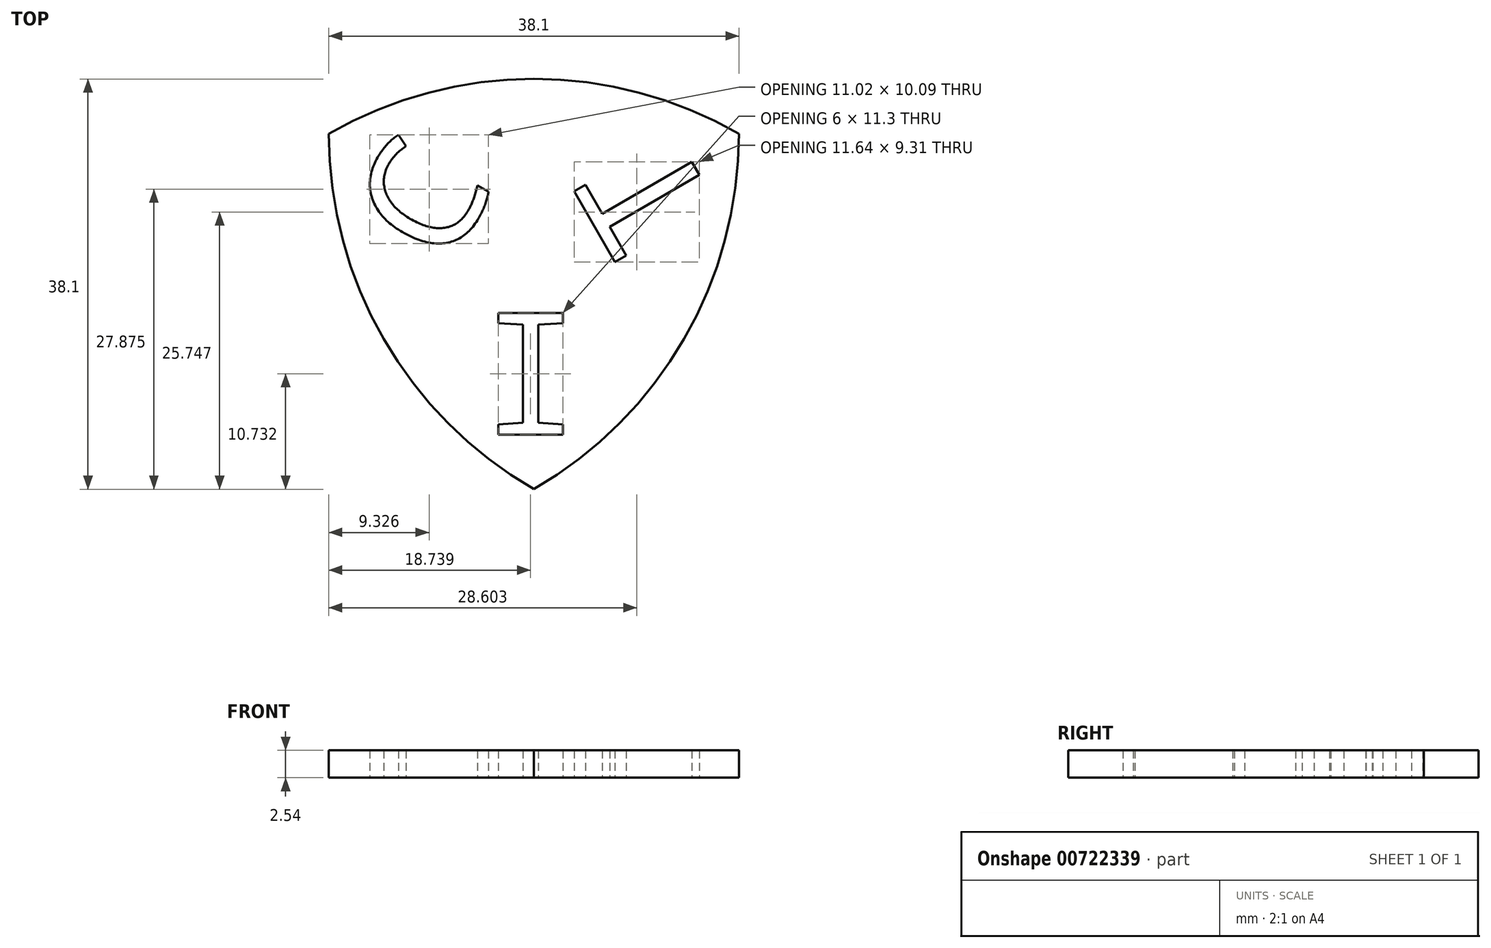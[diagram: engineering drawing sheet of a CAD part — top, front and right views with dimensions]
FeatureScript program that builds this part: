
annotation { "Feature Type Name" : "Feature", "Feature Type Description" : "" }
export const myFeature = defineFeature(function(context is Context, id is Id, definition is map)
    precondition{}
    {
        {
            var Q0;
            Q0=qCreatedBy(makeId("Top.planeOp"),FACE);
            var sketch = newSketch(context, id + "F0", { "sketchPlane" : qUnion([Q0])});
            skCircle(sketch, "E0", {"center": v(0, 0) * mm, "radius": 38.1 * mm});
            skSolve(sketch);
        }
        {
            var Q0;
            Q0=qCreatedBy(makeId("Top.planeOp"),FACE);
            var sketch = newSketch(context, id + "F1", { "sketchPlane" : qUnion([Q0])});
            skCircle(sketch, "E1", {"center": v(-38.1, 0) * mm, "radius": 38.1 * mm});
            skSolve(sketch);
        }
        {
            var Q0;
            Q0=qCreatedBy(makeId("Top.planeOp"),FACE);
            var sketch = newSketch(context, id + "F2", { "sketchPlane" : qUnion([Q0])});
            skCircle(sketch, "E2", {"center": v(-19.05, -33) * mm, "radius": 38.1 * mm});
            skSolve(sketch);
        }
        {
            var Q0;
            Q0 = qSketchRegion(id + "F0", true);
            extrude(context, id + "F3", {"entities" : qUnion([Q0]), "depth" : 2.54 * mm, "offsetDistance" : 25.4 * mm});
        }
        {
            var Q0;
            Q0 = qSketchRegion(id + "F1", true);
            extrude(context, id + "F4", {"entities" : qUnion([Q0]), "depth" : 2.54 * mm, "offsetDistance" : 25.4 * mm});
        }
        {
            var Q0;
            Q0 = qSketchRegion(id + "F2", true);
            extrude(context, id + "F5", {"entities" : qUnion([Q0]), "depth" : 2.54 * mm, "offsetDistance" : 25.4 * mm});
        }
        {
            var Q0;
            Q0=makeQuery(id+"F5.opExtrude","SWEPT_BODY",BODY,{"disambiguationData":[OSD([sQuery(id+"F2.wireOp",EDGE,"E2")])]});
            var Q1;
            Q1=makeQuery(id+"F4.opExtrude","SWEPT_BODY",BODY,{"disambiguationData":[OSD([sQuery(id+"F1.wireOp",EDGE,"E1")])]});
            var Q2;
            Q2=makeQuery(id+"F3.opExtrude","SWEPT_BODY",BODY,{"disambiguationData":[OSD([sQuery(id+"F0.wireOp",EDGE,"E0")])]});
            booleanBodies(context, id + "F6", {"operationType" : BooleanOperationType.INTERSECTION, "tools" : qUnion([Q0, Q1, Q2])});
        }
        {
            var Q0;
            Q0=qCreatedBy(makeId("Top.planeOp"),FACE);
            var sketch = newSketch(context, id + "F7", { "sketchPlane" : qUnion([Q0])});
            skText(sketch, "E3", { "text": "C", "fontName": "DroidSansMono.ttf"});
            skText(sketch, "E4", { "text": "I", "fontName": "DroidSansMono.ttf"});
            skText(sketch, "E5", { "text": "T", "fontName": "DroidSansMono.ttf"});
            const initialGuessF7  = {"E3": [-0.02711, -0.0126, 0.5, 0.86603, 0.01073], "E4": [-0.0241, -0.02792, 1, 0, 0.0114], "E5": [-0.00175, -0.00714, -0.5, 0.86603, 0.01094]};
            skSetInitialGuess(sketch, initialGuessF7);
            skSolve(sketch);
        }
        {
            var Q0;
            Q0 = qSketchRegion(id + "F7", true);
            extrude(context, id + "F8", {"entities" : qUnion([Q0]), "depth" : 2.54 * mm, "offsetDistance" : 25.4 * mm});
        }
        {
            var Q0;
            Q0=makeQuery(id+"F8.opExtrude","SWEPT_BODY",BODY,{"disambiguationData":[OSD([sQuery(id+"F7.wireOp",EDGE,"E3.sketch_text.stroke-0"),sQuery(id+"F7.wireOp",EDGE,"E3.sketch_text.stroke-1"),sQuery(id+"F7.wireOp",EDGE,"E3.sketch_text.stroke-2"),sQuery(id+"F7.wireOp",EDGE,"E3.sketch_text.stroke-3"),sQuery(id+"F7.wireOp",EDGE,"E3.sketch_text.stroke-4"),sQuery(id+"F7.wireOp",EDGE,"E3.sketch_text.stroke-5"),sQuery(id+"F7.wireOp",EDGE,"E3.sketch_text.stroke-6"),sQuery(id+"F7.wireOp",EDGE,"E3.sketch_text.stroke-7"),sQuery(id+"F7.wireOp",EDGE,"E3.sketch_text.stroke-8"),sQuery(id+"F7.wireOp",EDGE,"E3.sketch_text.stroke-9"),sQuery(id+"F7.wireOp",EDGE,"E3.sketch_text.stroke-10"),sQuery(id+"F7.wireOp",EDGE,"E3.sketch_text.stroke-11"),sQuery(id+"F7.wireOp",EDGE,"E3.sketch_text.stroke-12"),sQuery(id+"F7.wireOp",EDGE,"E3.sketch_text.stroke-13")])]});
            var Q1;
            Q1=makeQuery(id+"F8.opExtrude","SWEPT_BODY",BODY,{"disambiguationData":[OSD([sQuery(id+"F7.wireOp",EDGE,"E4.sketch_text.stroke-0"),sQuery(id+"F7.wireOp",EDGE,"E4.sketch_text.stroke-1"),sQuery(id+"F7.wireOp",EDGE,"E4.sketch_text.stroke-2"),sQuery(id+"F7.wireOp",EDGE,"E4.sketch_text.stroke-3"),sQuery(id+"F7.wireOp",EDGE,"E4.sketch_text.stroke-4"),sQuery(id+"F7.wireOp",EDGE,"E4.sketch_text.stroke-5"),sQuery(id+"F7.wireOp",EDGE,"E4.sketch_text.stroke-6"),sQuery(id+"F7.wireOp",EDGE,"E4.sketch_text.stroke-7"),sQuery(id+"F7.wireOp",EDGE,"E4.sketch_text.stroke-8"),sQuery(id+"F7.wireOp",EDGE,"E4.sketch_text.stroke-9"),sQuery(id+"F7.wireOp",EDGE,"E4.sketch_text.stroke-10"),sQuery(id+"F7.wireOp",EDGE,"E4.sketch_text.stroke-11")])]});
            var Q2;
            Q2=makeQuery(id+"F8.opExtrude","SWEPT_BODY",BODY,{"disambiguationData":[OSD([sQuery(id+"F7.wireOp",EDGE,"E5.sketch_text.stroke-0"),sQuery(id+"F7.wireOp",EDGE,"E5.sketch_text.stroke-1"),sQuery(id+"F7.wireOp",EDGE,"E5.sketch_text.stroke-2"),sQuery(id+"F7.wireOp",EDGE,"E5.sketch_text.stroke-3"),sQuery(id+"F7.wireOp",EDGE,"E5.sketch_text.stroke-4"),sQuery(id+"F7.wireOp",EDGE,"E5.sketch_text.stroke-5"),sQuery(id+"F7.wireOp",EDGE,"E5.sketch_text.stroke-6"),sQuery(id+"F7.wireOp",EDGE,"E5.sketch_text.stroke-7")])]});
            var Q3;
            Q3=makeQuery(id+"F6.opBoolean","INTERSECT",BODY,{"derivedFrom":[makeQuery(id+"F3.opExtrude","SWEPT_BODY",BODY,{"disambiguationData":[OSD([sQuery(id+"F0.wireOp",EDGE,"E0")])]}),makeQuery(id+"F4.opExtrude","SWEPT_BODY",BODY,{"disambiguationData":[OSD([sQuery(id+"F1.wireOp",EDGE,"E1")])]}),makeQuery(id+"F5.opExtrude","SWEPT_BODY",BODY,{"disambiguationData":[OSD([sQuery(id+"F2.wireOp",EDGE,"E2")])]})]});
            booleanBodies(context, id + "F9", {"operationType" : BooleanOperationType.SUBTRACTION, "tools" : qUnion([Q0, Q1, Q2]), "targets" : qUnion([Q3])});
        }
    });
